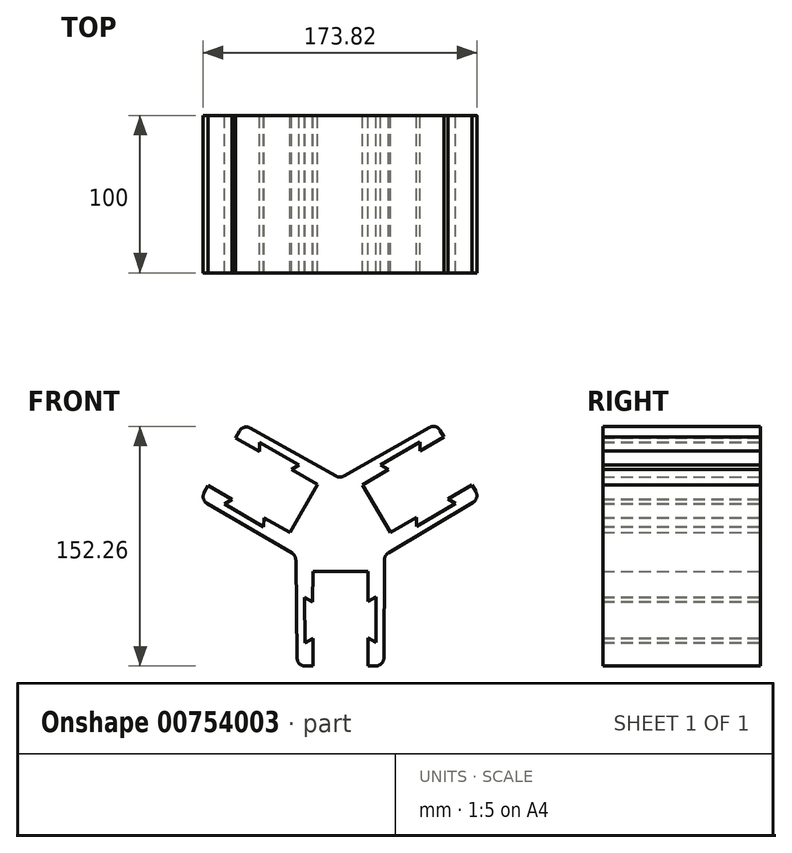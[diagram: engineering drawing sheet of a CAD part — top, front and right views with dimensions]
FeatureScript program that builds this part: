
annotation { "Feature Type Name" : "Feature", "Feature Type Description" : "" }
export const myFeature = defineFeature(function(context is Context, id is Id, definition is map)
    precondition{}
    {
        {
            var Q0;
            Q0=qCreatedBy(makeId("Front.planeOp"),FACE);
            var sketch = newSketch(context, id + "F0", { "sketchPlane" : qUnion([Q0])});
            skLineSegment(sketch, "E0.1", {"start": v(27.5, -123.04) * mm, "end": v(17.5, -123.07) * mm});
            skLineSegment(sketch, "E0.2", {"start": v(-149.93, -123.66) * mm, "end": v(-149.8, -123.42) * mm});
            skPoint(sketch, "E0.0.midPoint", {"position": v(74.61, 7.03) * mm});
            skLineSegment(sketch, "E1", {"start": v(-0.38, -3.92) * mm, "end": v(0, -123.13) * mm});
            skLineSegment(sketch, "E2", {"start": v(-28.44, -52.95) * mm, "end": v(22.76, -23.15) * mm});
            skLineSegment(sketch, "E3", {"start": v(27.98, -52.7) * mm, "end": v(-23.39, -23.27) * mm});
            skLineSegment(sketch, "E4.top", {"start": v(17.5, -63.13) * mm, "end": v(-17.5, -63.13) * mm});
            skLineSegment(sketch, "E4.left", {"start": v(17.5, -123.07) * mm, "end": v(17.5, -105.37) * mm});
            skPoint(sketch, "E4.middle", {"position": v(0, -123.13) * mm});
            skPoint(sketch, "E4.bottom.end.orphan", {"position": v(-17.5, -183.13) * mm});
            skPoint(sketch, "E5.orphan", {"position": v(17.5, -183.13) * mm});
            skPoint(sketch, "E6", {"position": v(17.5, -93.1) * mm});
            skLineSegment(sketch, "E7", {"start": v(22.5, -79.32) * mm, "end": v(22.5, -108.23) * mm});
            skLineSegment(sketch, "E8", {"start": v(22.5, -108.23) * mm, "end": v(17.5, -105.37) * mm});
            skLineSegment(sketch, "E9.MirrorCS", {"start": v(-22.78, -79.47) * mm, "end": v(-22.6, -108.37) * mm});
            skLineSegment(sketch, "E10.MirrorCS", {"start": v(-22.6, -108.37) * mm, "end": v(-17.61, -105.48) * mm});
            skPoint(sketch, "E11", {"position": v(27.5, -123.04) * mm});
            skPoint(sketch, "E12", {"position": v(22.5, -93.78) * mm});
            skLineSegment(sketch, "E13.MirrorCS", {"start": v(22.5, -79.32) * mm, "end": v(17.5, -82.19) * mm});
            skLineSegment(sketch, "E14.MirrorCS", {"start": v(-22.78, -79.47) * mm, "end": v(-17.76, -82.3) * mm});
            skPoint(sketch, "E15.MirrorCS.end.orphan", {"position": v(-22.78, -79.47) * mm});
            skPoint(sketch, "E15.MirrorCS.start.orphan", {"position": v(-17.75, -84.61) * mm});
            skLineSegment(sketch, "E16.MirrorCS", {"start": v(31.68, -38.37) * mm, "end": v(13.97, -8.18) * mm});
            skLineSegment(sketch, "E17.MirrorCS", {"start": v(83.38, -8.04) * mm, "end": v(68.11, -17) * mm});
            skLineSegment(sketch, "E18.MirrorCS", {"start": v(25.39, 4.64) * mm, "end": v(50.42, 19.11) * mm});
            skLineSegment(sketch, "E19.MirrorCS", {"start": v(25.39, 4.64) * mm, "end": v(30.37, 1.75) * mm});
            skLineSegment(sketch, "E20.MirrorCS", {"start": v(50.42, 19.11) * mm, "end": v(50.44, 13.35) * mm});
            skLineSegment(sketch, "E21.MirrorCS", {"start": v(73.11, -19.86) * mm, "end": v(68.11, -17) * mm});
            skLineSegment(sketch, "E22.MirrorCS", {"start": v(48.18, -34.49) * mm, "end": v(73.11, -19.86) * mm});
            skLineSegment(sketch, "E23.MirrorCS", {"start": v(48.18, -34.49) * mm, "end": v(48.12, -28.72) * mm});
            skLineSegment(sketch, "E24", {"start": v(27.5, -123.04) * mm, "end": v(27.98, -52.7) * mm});
            skLineSegment(sketch, "E25.MirrorCS", {"start": v(-27.5, -123.21) * mm, "end": v(-28.44, -52.87) * mm});
            skLineSegment(sketch, "E26.MirrorCS", {"start": v(-150.07, -123.58) * mm, "end": v(-149.8, -123.42) * mm});
            skLineSegment(sketch, "E27.MirrorCS", {"start": v(88.41, -16.68) * mm, "end": v(27.98, -52.7) * mm});
            skLineSegment(sketch, "E28.MirrorCS", {"start": v(60.74, 30.85) * mm, "end": v(-0.4, -3.93) * mm});
            skLineSegment(sketch, "E29.MirrorCS", {"start": v(-89.1, -17.25) * mm, "end": v(-28.44, -52.87) * mm});
            skLineSegment(sketch, "E30.MirrorCS", {"start": v(-48.75, -34.8) * mm, "end": v(-73.78, -20.33) * mm});
            skLineSegment(sketch, "E31.MirrorCS", {"start": v(-84.13, -8.57) * mm, "end": v(-84.05, -8.62) * mm});
            skLineSegment(sketch, "E32.MirrorCS", {"start": v(-14.62, -7.88) * mm, "end": v(-31.94, -38.3) * mm});
            skLineSegment(sketch, "E33.MirrorCS", {"start": v(-48.75, -34.8) * mm, "end": v(-48.73, -29.04) * mm});
            skLineSegment(sketch, "E34.MirrorCS", {"start": v(-73.78, -20.33) * mm, "end": v(-68.8, -17.44) * mm});
            skLineSegment(sketch, "E35.MirrorCS", {"start": v(-66.7, 21.78) * mm, "end": v(-51.32, 13.02) * mm});
            skLineSegment(sketch, "E36.MirrorCS", {"start": v(-26.21, 4.48) * mm, "end": v(-51.33, 18.78) * mm});
            skLineSegment(sketch, "E37.MirrorCS", {"start": v(-51.33, 18.78) * mm, "end": v(-51.32, 13.02) * mm});
            skLineSegment(sketch, "E38.MirrorCS", {"start": v(-26.21, 4.48) * mm, "end": v(-31.18, 1.55) * mm});
            skLineSegment(sketch, "E39.MirrorCS", {"start": v(-61.73, 30.46) * mm, "end": v(-0.36, -3.93) * mm});
            skLineSegment(sketch, "E40.trimOffspring", {"start": v(-89.02, -17.3) * mm, "end": v(-84.05, -8.62) * mm});
            skLineSegment(sketch, "E41.trimOffspring", {"start": v(-28.44, -52.87) * mm, "end": v(22.74, -23.12) * mm});
            skPoint(sketch, "E42.orphan", {"position": v(150.07, -122.61) * mm});
            skLineSegment(sketch, "E43.trimOffspring", {"start": v(83.38, -8.04) * mm, "end": v(88.41, -16.68) * mm});
            skLineSegment(sketch, "E44.trimOffspring", {"start": v(74.58, 7.01) * mm, "end": v(75.46, 7.52) * mm});
            skPoint(sketch, "E45.MirrorCS.end.orphan", {"position": v(13.97, -8.18) * mm});
            skLineSegment(sketch, "E46.trimOffspring", {"start": v(74.58, 7.01) * mm, "end": v(74.61, 7.03) * mm});
            skLineSegment(sketch, "E47.trimOffspring", {"start": v(48.12, -28.72) * mm, "end": v(31.68, -38.37) * mm});
            skPoint(sketch, "E48.end.orphan", {"position": v(17.5, -84.5) * mm});
            skLineSegment(sketch, "E49.trimOffspring", {"start": v(17.5, -82.19) * mm, "end": v(17.5, -63.13) * mm});
            skPoint(sketch, "E50.trimOffspring.end.orphan", {"position": v(-17.5, -123.2) * mm});
            skLineSegment(sketch, "E51", {"start": v(-17.5, -63.13) * mm, "end": v(-17.76, -82.3) * mm});
            skLineSegment(sketch, "E52", {"start": v(-17.61, -105.48) * mm, "end": v(-17.5, -123.2) * mm});
            skLineSegment(sketch, "E53", {"start": v(-27.5, -123.21) * mm, "end": v(-17.5, -123.2) * mm});
            skLineSegment(sketch, "E54", {"start": v(13.97, -8.18) * mm, "end": v(30.37, 1.75) * mm});
            skLineSegment(sketch, "E55", {"start": v(50.44, 13.35) * mm, "end": v(65.78, 22.21) * mm});
            skPoint(sketch, "E0.0.start.orphan", {"position": v(-0.84, 136.67) * mm});
            skLineSegment(sketch, "E56.trimOffspring", {"start": v(-66.65, 21.75) * mm, "end": v(-61.68, 30.43) * mm});
            skPoint(sketch, "E57.orphan", {"position": v(-76.3, 7.03) * mm});
            skLineSegment(sketch, "E58.trimOffspring", {"start": v(-31.18, 1.55) * mm, "end": v(-14.62, -7.88) * mm});
            skPoint(sketch, "E59.orphan", {"position": v(-31.94, -38.3) * mm});
            skLineSegment(sketch, "E60", {"start": v(-84.05, -8.62) * mm, "end": v(-68.8, -17.44) * mm});
            skLineSegment(sketch, "E61", {"start": v(-48.73, -29.04) * mm, "end": v(-31.94, -38.3) * mm});
            skLineSegment(sketch, "E62", {"start": v(60.74, 30.85) * mm, "end": v(65.78, 22.21) * mm});
            skSolve(sketch);
        }
        {
            var Q0;
            Q0=makeQuery(id+"F0.imprint","IMPRINT",FACE,{"disambiguationData":[TD([[makeQuery(id+"F0.imprint","IMPRINT",EDGE,{"derivedFrom":sQuery(id+"F0.wireOp",EDGE,"E18.MirrorCS")}),1.0]])]});
            var Q1;
            Q1=makeQuery(id+"F0.imprint","IMPRINT",FACE,{"disambiguationData":[TD([[makeQuery(id+"F0.imprint","IMPRINT",EDGE,{"derivedFrom":sQuery(id+"F0.wireOp",EDGE,"E0.1")}),-1.0]])]});
            var Q2;
            Q2=makeQuery(id+"F0.imprint","IMPRINT",FACE,{"disambiguationData":[TD([[makeQuery(id+"F0.imprint","IMPRINT",EDGE,{"derivedFrom":sQuery(id+"F0.wireOp",EDGE,"E17.MirrorCS")}),1.0]])]});
            var Q3;
            {var subQ0=sQuery(id+"F0.wireOp",EDGE,"E2");var subQ5=sQuery(id+"F0.wireOp",EDGE,"E25.MirrorCS");var subQ6=makeQuery(id+"F0.imprint","INTERSECT",VERTEX,{"derivedFrom":[subQ0,subQ5]});Q3=makeQuery(id+"F0.imprint","IMPRINT",FACE,{"disambiguationData":[TD([[makeQuery(id+"F0.imprint","IMPRINT",EDGE,{"disambiguationData":[TD([[subQ6,-1.0]])],"derivedFrom":subQ0}),1.0]])]});}
            var Q4;
            Q4=makeQuery(id+"F0.imprint","IMPRINT",FACE,{"disambiguationData":[TD([[makeQuery(id+"F0.imprint","IMPRINT",EDGE,{"derivedFrom":sQuery(id+"F0.wireOp",EDGE,"E9.MirrorCS")}),-1.0]])]});
            var Q5;
            Q5=makeQuery(id+"F0.imprint","IMPRINT",FACE,{"disambiguationData":[TD([[makeQuery(id+"F0.imprint","IMPRINT",EDGE,{"derivedFrom":sQuery(id+"F0.wireOp",EDGE,"E36.MirrorCS")}),-1.0]])]});
            var Q6;
            Q6=makeQuery(id+"F0.imprint","IMPRINT",FACE,{"disambiguationData":[TD([[makeQuery(id+"F0.imprint","IMPRINT",EDGE,{"derivedFrom":sQuery(id+"F0.wireOp",EDGE,"E30.MirrorCS")}),1.0]])]});
            var Q7;
            {var subQ0=sQuery(id+"F0.wireOp",EDGE,"E16.MirrorCS");var subQ1=sQuery(id+"F0.wireOp",EDGE,"E2");var subQ2=makeQuery(id+"F0.imprint","INTERSECT",VERTEX,{"derivedFrom":[subQ1,subQ0]});Q7=makeQuery(id+"F0.imprint","IMPRINT",FACE,{"disambiguationData":[TD([[makeQuery(id+"F0.imprint","IMPRINT",EDGE,{"disambiguationData":[TD([[subQ2,1.0]])],"derivedFrom":subQ1}),1.0]])]});}
            var Q8;
            {var subQ0=sQuery(id+"F0.wireOp",EDGE,"E2");var subQ1=sQuery(id+"F0.wireOp",EDGE,"E1");var subQ2=makeQuery(id+"F0.imprint","INTERSECT",VERTEX,{"derivedFrom":[subQ1,subQ0]});Q8=makeQuery(id+"F0.imprint","IMPRINT",FACE,{"disambiguationData":[TD([[makeQuery(id+"F0.imprint","IMPRINT",EDGE,{"disambiguationData":[TD([[subQ2,-1.0]])],"derivedFrom":subQ0}),1.0]])]});}
            extrude(context, id + "F1", {"entities" : qUnion([Q0, Q1, Q2, Q3, Q4, Q5, Q6, Q7, Q8]), "endBound" : BoundingType.SYMMETRIC, "depth" : 100 * mm, "offsetDistance" : 25.4 * mm});
        }
        {
            var Q0;
            Q0=makeQuery(id+"F1.opExtrude","SWEPT_EDGE",EDGE,{"disambiguationData":[OSD([sQuery(id+"F0.wireOp",EDGE,"E39.MirrorCS"),sQuery(id+"F0.wireOp",EDGE,"E56.trimOffspring")])]});
            var Q1;
            Q1=makeQuery(id+"F1.opExtrude","SWEPT_EDGE",EDGE,{"disambiguationData":[OSD([sQuery(id+"F0.wireOp",EDGE,"E28.MirrorCS"),sQuery(id+"F0.wireOp",EDGE,"E62")])]});
            var Q2;
            Q2=makeQuery(id+"F1.opExtrude","SWEPT_EDGE",EDGE,{"disambiguationData":[OSD([sQuery(id+"F0.wireOp",EDGE,"E1"),sQuery(id+"F0.wireOp",EDGE,"E28.MirrorCS"),sQuery(id+"F0.wireOp",EDGE,"E39.MirrorCS")])]});
            var Q3;
            Q3=makeQuery(id+"F1.opExtrude","SWEPT_EDGE",EDGE,{"disambiguationData":[OSD([sQuery(id+"F0.wireOp",EDGE,"E27.MirrorCS"),sQuery(id+"F0.wireOp",EDGE,"E43.trimOffspring")])]});
            var Q4;
            Q4=makeQuery(id+"F1.opExtrude","SWEPT_EDGE",EDGE,{"disambiguationData":[OSD([sQuery(id+"F0.wireOp",EDGE,"E0.1"),sQuery(id+"F0.wireOp",EDGE,"E24")])]});
            var Q5;
            Q5=makeQuery(id+"F1.opExtrude","SWEPT_EDGE",EDGE,{"disambiguationData":[OSD([sQuery(id+"F0.wireOp",EDGE,"E3"),sQuery(id+"F0.wireOp",EDGE,"E24"),sQuery(id+"F0.wireOp",EDGE,"E27.MirrorCS")])]});
            var Q6;
            Q6=makeQuery(id+"F1.opExtrude","SWEPT_EDGE",EDGE,{"disambiguationData":[OSD([sQuery(id+"F0.wireOp",EDGE,"E25.MirrorCS"),sQuery(id+"F0.wireOp",EDGE,"E53")])]});
            var Q7;
            Q7=makeQuery(id+"F1.opExtrude","SWEPT_EDGE",EDGE,{"disambiguationData":[OSD([sQuery(id+"F0.wireOp",EDGE,"E25.MirrorCS"),sQuery(id+"F0.wireOp",EDGE,"E29.MirrorCS"),sQuery(id+"F0.wireOp",EDGE,"E41.trimOffspring")])]});
            var Q8;
            Q8=makeQuery(id+"F1.opExtrude","SWEPT_EDGE",EDGE,{"disambiguationData":[OSD([sQuery(id+"F0.wireOp",EDGE,"E29.MirrorCS"),sQuery(id+"F0.wireOp",EDGE,"E40.trimOffspring")])]});
            fillet(context, id + "F2", {"entities" : qUnion([Q0, Q1, Q2, Q3, Q4, Q5, Q6, Q7, Q8]), "radius" : 5 * mm, "tangentPropagation" : true, "allowEdgeOverflow" : false});
        }
    });
